# Revit family: Indirect-Water-Heater_AO_Smith-IT-500_F_B
name_source: partatom
category: Mechanical Equipment
revit_build: Autodesk Revit 2016 (Build: 20170117_1200(x64)
units: mm (PartAtom-declared; Revit-internal decimal feet)

## family parameters
Always vertical = Yes
Cut with Voids When Loaded = No
OmniClass Number = 23.75.00.00
OmniClass Title = Climate Control (HVAC)
Part Type = Normal
Room Calculation Point = No
Round Connector Dimension = Use Radius
Shared = No
Work Plane-Based = No

## types (1)
- Indirect-Water-Heater_AO_Smith-IT-500_F_B
    1er Entretien (check-up) = 3 mois après l'installation
    2ème Entretien (Entretien Général) = 12 mois après l'installation
    Assembly Code = D3010
    BIM Content Developer = CAD & Company
    BIM Content Developer URL = http://www.cadcompany.nl
    Capacité - Cuve = 473 m³
    Capacité - Échangeur Inférieur = 18.8 m³
    Charge Maximale au Sol = 653.00 kg
    Description = Cuve Indirects Fournis d’un Échangeur
    Destination / Pays = France
    Diamètre (avec Isolation) = 760 mm  [stored 2.49344 ft]
    Diamètre (sans Isolation) = 600 mm  [stored 1.9685 ft]
    Débit de vidage en Continu à ΔT = 28°C = 3071
    Débit de vidage en Continu à ΔT = 44°C = 1955
    Débit de vidage en Continu à ΔT = 50°C = 1720
    Débit de vidage en Continu à ΔT = 55°C = 1564
    Débit de vidage en Continu à ΔT = 70°C = 1229
    Débit de vidage à ΔT = 28°C après 120 min. = 6935.0 L
    Débit de vidage à ΔT = 28°C après 30 min. = 2328.0 L
    Débit de vidage à ΔT = 28°C après 60 min. = 3864.0 L
    Débit de vidage à ΔT = 28°C après 90 min. = 5400.0 L
    Débit de vidage à ΔT = 44°C après 120 min. = 4413.0 L
    Débit de vidage à ΔT = 44°C après 30 min. = 1482.0 L
    Débit de vidage à ΔT = 44°C après 60 min. = 2459.0 L
    Débit de vidage à ΔT = 44°C après 90 min. = 3436.0 L
    Débit de vidage à ΔT = 50°C après 120 min. = 3884.0 L
    Débit de vidage à ΔT = 50°C après 30 min. = 1304.0 L
    Débit de vidage à ΔT = 50°C après 60 min. = 2164.0 L
    Débit de vidage à ΔT = 50°C après 90 min. = 3024.0 L
    Débit de vidage à ΔT = 55°C après 120 min. = 3531.0 L
    Débit de vidage à ΔT = 55°C après 30 min. = 1185.0 L
    Débit de vidage à ΔT = 55°C après 60 min. = 1967.0 L
    Débit de vidage à ΔT = 55°C après 90 min. = 2749.0 L
    Débit de vidage à ΔT = 70°C après 120 min. = 2774.0 L
    Débit de vidage à ΔT = 70°C après 30 min. = 931.0 L
    Débit de vidage à ΔT = 70°C après 60 min. = 1546.0 L
    Débit de vidage à ΔT = 70°C après 90 min. = 2160.0 L
    Débit à 80ºC/60ºC - Échangeur Inférieur = 4300
    Epaisseur d'Isolation = 80 mm  [stored 0.262467 ft]
    Fabricant No. = E 7110
    Garantie Pièces = 12 mois
    Garantie sur la Cuve = 36 mois
    Guide de Produit = https://www.aosmithinternational.com
    Hauteur (avec Isolation) = 2045 mm  [stored 6.70932 ft]
    Hauteur (sans Isolation) = 1995 mm  [stored 6.54528 ft]
    Hauteur d'Emballage = 2150 mm
    Hauteur de l'Alimentation en eau Froide = 70 mm  [stored 0.229659 ft]
    Hauteur de la Sortie d'eau Chaude = 1995 mm  [stored 6.54528 ft]
    Largeur d'Emballage = 780 mm  [stored 2.55906 ft]
    Manufacturer = A.O. Smith Water Products Company b.v.
    Max. Température de l'eau - Réservoir = 95 °C
    Model = IT 500 F B
    Nombre de modèle du produit (EAN) = 8717449181451
    Perte de Pression à 80ºC/60ºC - Échangeur Inférieur = 48900.0 Pa
    Pertes en Veille = 0 W
    Pertes en Veille - tous les jours (24h) = 0
    Poids de Transport = 201.00 kg
    Poids à vide = 180.00 kg
    Pression de Service Maximale - Réservoir = 1000000.0 Pa
    Pression de Service Maximale - Échangeur Inférieur = 1600000.0 Pa
    Production Nominale - Échangeur Inférieur = 100000 W
    Profondeur d'Emballage = 780 mm  [stored 2.55906 ft]
    Raccord d'Alimentation en Eau Froide = 2"
    Raccord de Sortie d'Eau Chaude = 2"
    Raccord de la Soupape de Vidange = 1"
    Spécifications du Produit = https://www.aosmithinternational.com
    Surface d'Échange de Chaleur - Échangeur Inférieur = 3.11 m²
    Temps de réchauffement à ΔT = 28°C = 9
    Temps de réchauffement à ΔT = 44°C = 15
    Temps de réchauffement à ΔT = 50°C = 16
    Temps de réchauffement à ΔT = 55°C = 18
    Temps de réchauffement à ΔT = 70°C = 23
    Température Maximale - Échangeur Inférieur = 110 °C
    Type d'Emballage = Plastique et Bois
    URL = http://www.aosmith.fr
    Workspace Diameter = 1760 mm  [stored 5.77428 ft]
    Workspace Height = 3045 mm
    espace de travail = 860 mm
    l'Intervalle d'Entretien = 12 mois

note: [stored X ft] marks values corroborated as IEEE doubles in the binary element streams (Revit-internal decimal feet)

## geometry (parser evidence)
native form markers: Blend x2, Sweep x21
no freeform markers — native parametric forms only
